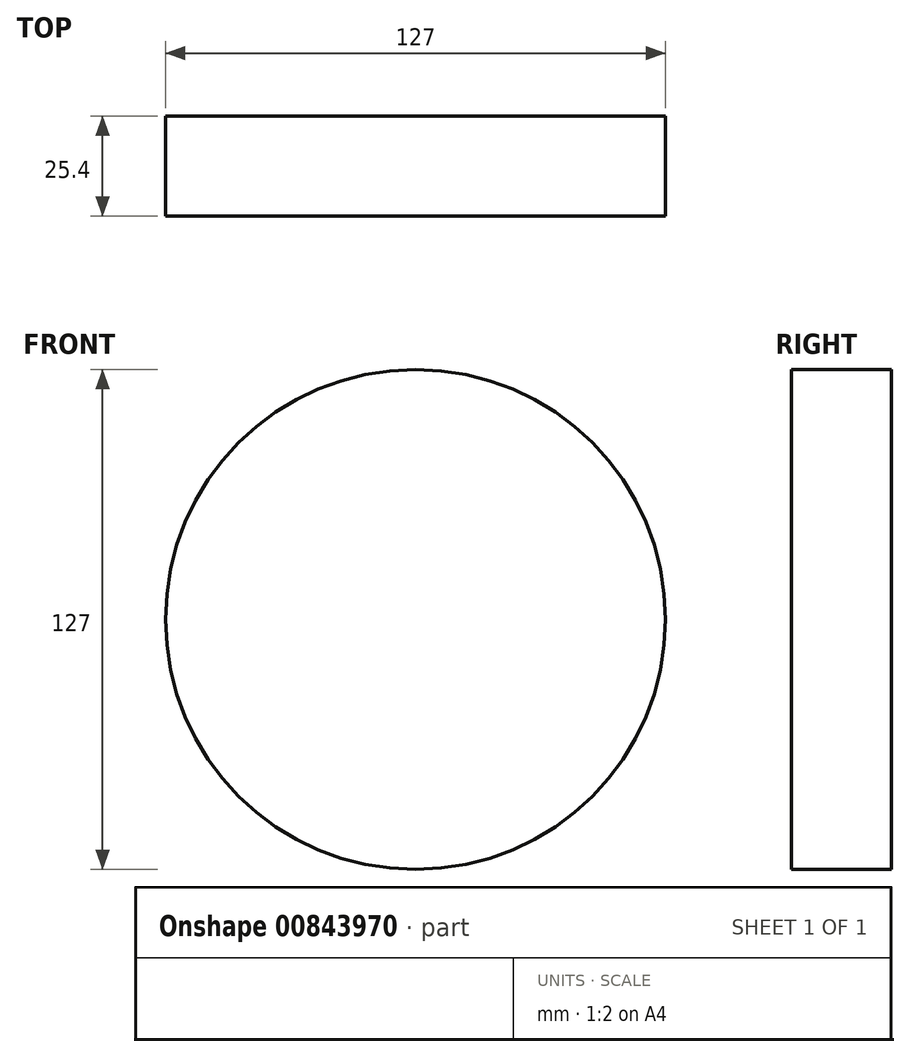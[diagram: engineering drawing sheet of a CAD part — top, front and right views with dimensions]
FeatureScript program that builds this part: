
annotation { "Feature Type Name" : "Feature", "Feature Type Description" : "" }
export const myFeature = defineFeature(function(context is Context, id is Id, definition is map)
    precondition{}
    {
        {
            var Q0;
            Q0=qCreatedBy(makeId("Front.planeOp"),FACE);
            var sketch = newSketch(context, id + "F0", { "sketchPlane" : qUnion([Q0])});
            skCircle(sketch, "E0", {"center": v(0, 0) * mm, "radius": 63.5 * mm});
            skCircle(sketch, "E1", {"center": v(0, 0) * mm, "radius": 50.8 * mm});
            skSolve(sketch);
        }
        {
            var Q0;
            Q0=makeQuery(id+"F0.imprint","IMPRINT",FACE,{"disambiguationData":[TD([[makeQuery(id+"F0.imprint","IMPRINT",EDGE,{"derivedFrom":sQuery(id+"F0.wireOp",EDGE,"E0")}),1.0]])]});
            var Q1;
            Q1=makeQuery(id+"F0.imprint","IMPRINT",FACE,{"disambiguationData":[TD([[makeQuery(id+"F0.imprint","IMPRINT",EDGE,{"derivedFrom":sQuery(id+"F0.wireOp",EDGE,"E1")}),1.0]])]});
            extrude(context, id + "F1", {"entities" : qUnion([Q0, Q1]), "depth" : 25.4 * mm, "offsetDistance" : 25.4 * mm});
        }
    });
